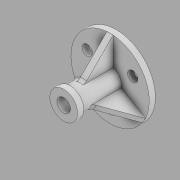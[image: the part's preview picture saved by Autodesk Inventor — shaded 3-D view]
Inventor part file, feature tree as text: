
AUTODESK INVENTOR PART (.ipt)
format: ipt  version: 2020 (Build 240168000, 168)  size: 206,848 bytes
history: native  units: mm
features: sketch x7, other x4, extrude x3, plane x2, hole x1, fillet x1
ambient origin geometry x8: Origin, YZ Plane, XZ Plane, XY Plane, X Axis, Y Axis, Z Axis, Center Point
bodies: Body1 (feature_tree)
feature tree (18):
  other  "Sólido1"
  extrude  "Extrusión1"  Depth=102.0mm
  extrude  "Extrusión2"  Depth=20.0mm
  extrude  "Extrusión3"  Depth=12.0mm TaperAngle=0.0deg
  other  "Nervio1"
  plane  "Plano de trabajo2"
  plane  "Plano de trabajo3"
  other  "Nervio3"
  other  "Nervio4"
  hole  "Agujero1"  [1 undecoded]
  fillet  "Empalme1"  Radius=54.0mm
  sketch  "Boceto1"  dims[d0=152.0mm d1=102.0mm]
  sketch  "Boceto2"  dims[d3=30.0deg d4=20.0mm]
  sketch  "Boceto3"  dims[d5=30.0mm d7=360.0deg d9=12.0mm d10=0.0mm]
  sketch  "Boceto4"  dims[d11=44.0mm d12=78.0mm d13=0.0mm d14=54.0mm]
  sketch  "Boceto6"  dims[d15=12.0mm d16=0.0mm]
  sketch  "Boceto7"  dims[d17=45.0deg]
  sketch  "Boceto8"  dims[d18=1.0mm d19=12.0mm d20=0.0mm d21=0.0mm d22=1.0mm d23=1.0mm d33=120.0deg d34=60.0deg d35=45.0deg d36=1.0mm d37=12.0mm d38=0.0mm d39=0.0mm d40=1.0mm d41=1.0mm d42=45.0deg d43=1.0mm d44=12.0mm d45=0.0mm d46=0.0mm d47=1.0mm d48=1.0mm d49=26.0mm d50=6.0mm d51=4.0mm d52=2.0mm d53=90.0deg d54=8.0mm d55=20.594885mm d56=10.0mm]
note: 1 required parameter value undecoded (feature->parameter linkage not recoverable at this tier; creation-order binding heuristic only, values carry confidence <= 0.55)
